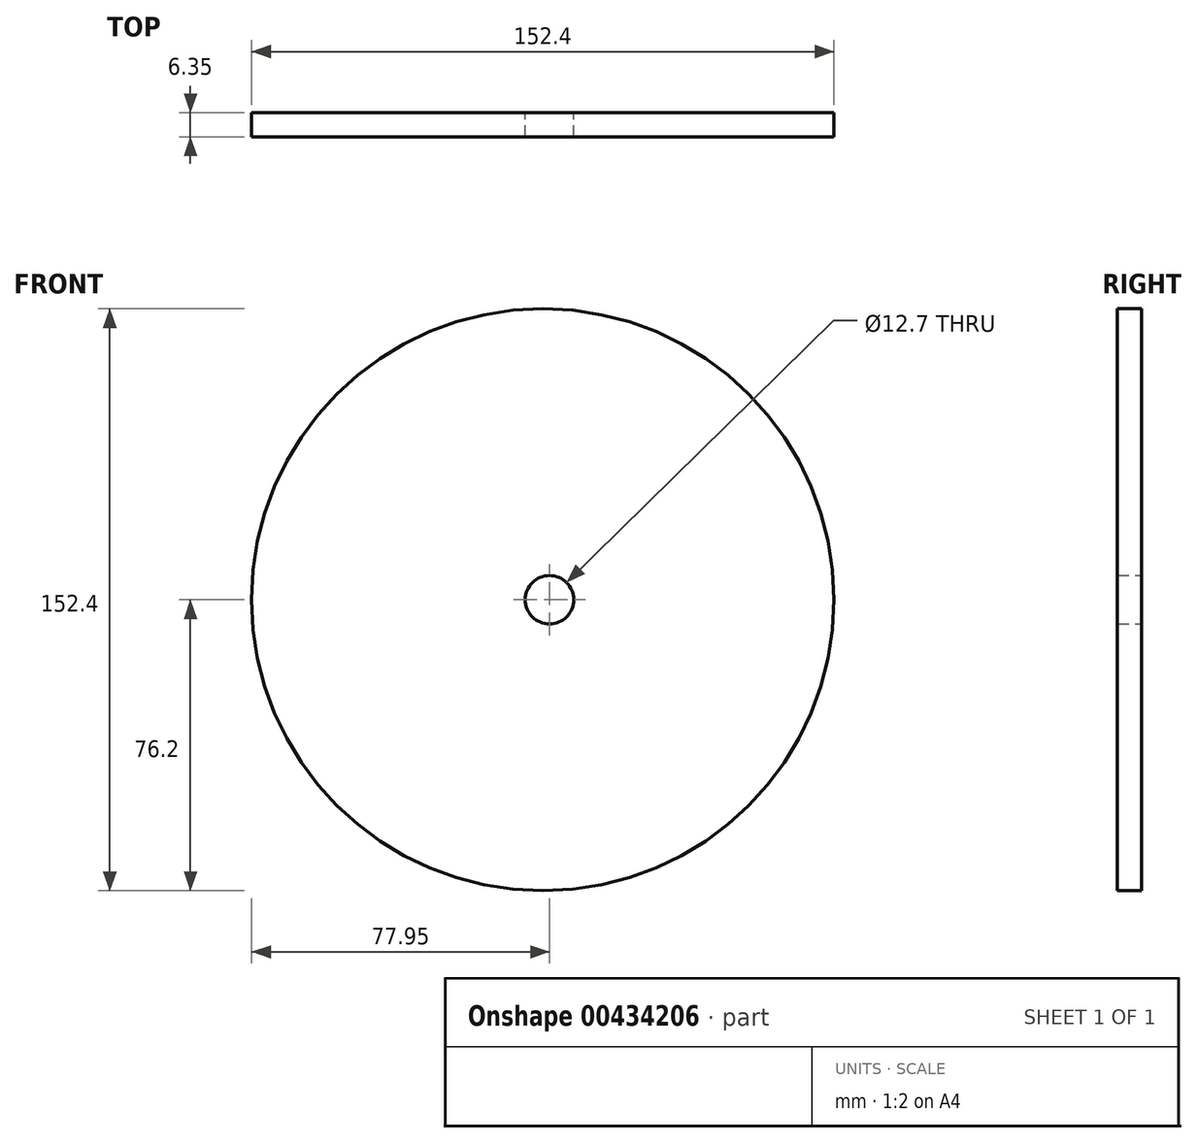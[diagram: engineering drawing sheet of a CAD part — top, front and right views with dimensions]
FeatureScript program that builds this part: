
annotation { "Feature Type Name" : "Feature", "Feature Type Description" : "" }
export const myFeature = defineFeature(function(context is Context, id is Id, definition is map)
    precondition{}
    {
        {
            var Q0;
            Q0=qCreatedBy(makeId("Front.planeOp"),FACE);
            var sketch = newSketch(context, id + "F0", { "sketchPlane" : qUnion([Q0])});
            skCircle(sketch, "E0", {"center": v(0, 0) * mm, "radius": 6.35 * mm});
            skCircle(sketch, "E1", {"center": v(-1.75, 0) * mm, "radius": 76.2 * mm});
            skSolve(sketch);
        }
        {
            var Q0;
            Q0 = qSketchRegion(id + "F0", true);
            extrude(context, id + "F1", {"entities" : qUnion([Q0]), "depth" : 6.35 * mm});
        }
    });
